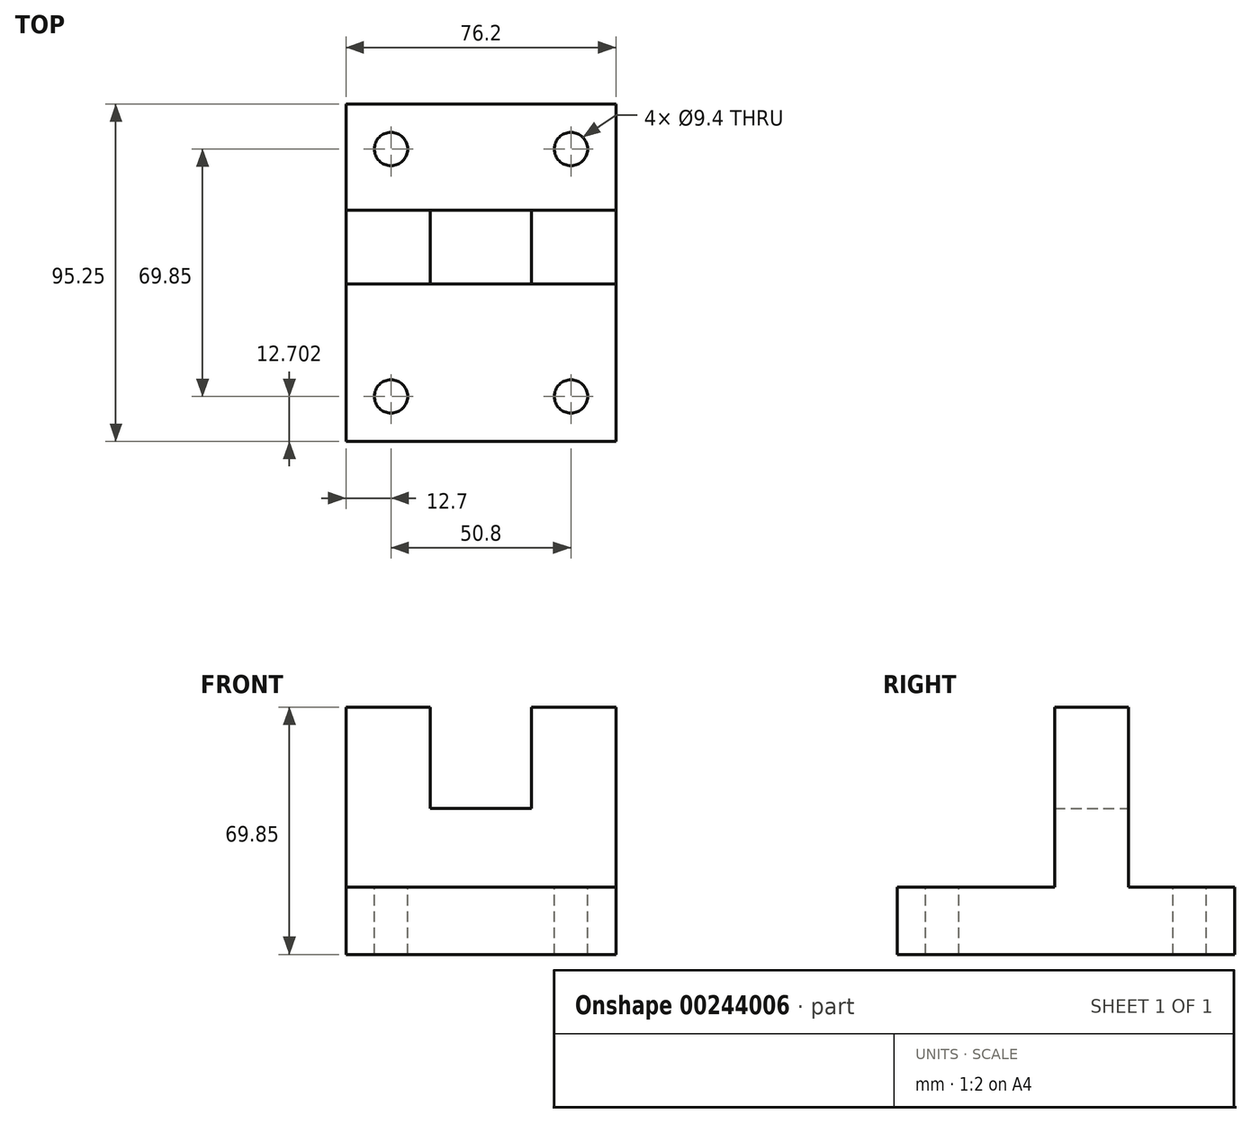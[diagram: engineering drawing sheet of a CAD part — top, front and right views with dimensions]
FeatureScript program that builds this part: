
annotation { "Feature Type Name" : "Feature", "Feature Type Description" : "" }
export const myFeature = defineFeature(function(context is Context, id is Id, definition is map)
    precondition{}
    {
        {
            var Q0;
            Q0=qCreatedBy(makeId("Front.planeOp"),FACE);
            var sketch = newSketch(context, id + "F0", { "sketchPlane" : qUnion([Q0])});
            skLineSegment(sketch, "E0.bottom", {"start": v(-52.39, 0) * mm, "end": v(-23.81, 0) * mm});
            skLineSegment(sketch, "E0.top", {"start": v(-76.2, -3.18) * mm, "end": v(0, -3.18) * mm});
            skLineSegment(sketch, "E0.left", {"start": v(-76.2, 0) * mm, "end": v(-76.2, -3.18) * mm});
            skLineSegment(sketch, "E0.right", {"start": v(0, 0) * mm, "end": v(0, -3.18) * mm});
            skLineSegment(sketch, "E1.bottom", {"start": v(-76.2, 28.58) * mm, "end": v(-52.39, 28.58) * mm});
            skLineSegment(sketch, "E1.left", {"start": v(-76.2, 28.58) * mm, "end": v(-76.2, 0) * mm});
            skLineSegment(sketch, "E1.right", {"start": v(-52.39, 28.58) * mm, "end": v(-52.39, 0) * mm});
            skLineSegment(sketch, "E2.top", {"start": v(-23.81, 28.58) * mm, "end": v(0, 28.58) * mm});
            skLineSegment(sketch, "E2.left", {"start": v(-23.81, 0) * mm, "end": v(-23.81, 28.58) * mm});
            skLineSegment(sketch, "E2.right", {"start": v(0, 0) * mm, "end": v(0, 28.58) * mm});
            skLineSegment(sketch, "E3.top", {"start": v(-76.2, -22.23) * mm, "end": v(0, -22.23) * mm});
            skLineSegment(sketch, "E3.left", {"start": v(-76.2, -3.18) * mm, "end": v(-76.2, -22.23) * mm});
            skLineSegment(sketch, "E3.right", {"start": v(0, -3.18) * mm, "end": v(0, -22.23) * mm});
            skSolve(sketch);
        }
        {
            var Q0;
            Q0 = qSketchRegion(id + "F0", true);
            extrude(context, id + "F1", {"entities" : qUnion([Q0]), "depth" : 20.83 * mm});
        }
        {
            var Q0;
            Q0=qCreatedBy(makeId("Right.planeOp"),FACE);
            var sketch = newSketch(context, id + "F2", { "sketchPlane" : qUnion([Q0])});
            skPoint(sketch, "E4.end.orphan", {"position": v(-65.73, -22.57) * mm});
            skPoint(sketch, "E5.start.orphan", {"position": v(-65.73, -41.62) * mm});
            skPoint(sketch, "E6.start.orphan", {"position": v(0, -22.57) * mm});
            skPoint(sketch, "E7.end.orphan", {"position": v(29.52, -41.62) * mm});
            skLineSegment(sketch, "E8.0", {"start": v(-20.83, -22.23) * mm, "end": v(0, -22.23) * mm});
            skLineSegment(sketch, "E9", {"start": v(-20.83, -22.23) * mm, "end": v(-65.28, -22.23) * mm});
            skLineSegment(sketch, "E10", {"start": v(-65.28, -22.23) * mm, "end": v(-65.28, -41.28) * mm});
            skLineSegment(sketch, "E11", {"start": v(-65.28, -41.28) * mm, "end": v(29.97, -41.28) * mm});
            skLineSegment(sketch, "E12", {"start": v(29.97, -41.28) * mm, "end": v(29.97, -22.23) * mm});
            skLineSegment(sketch, "E13", {"start": v(29.97, -22.23) * mm, "end": v(0, -22.23) * mm});
            skSolve(sketch);
        }
        {
            var Q0;
            Q0 = qSketchRegion(id + "F2", true);
            extrude(context, id + "F3", {"entities" : qUnion([Q0]), "operationType" : NewBodyOperationType.ADD, "oppositeDirection" : true, "depth" : 76.2 * mm});
        }
        {
            var Q0;
            Q0=qCreatedBy(makeId("Top.planeOp"),FACE);
            var sketch = newSketch(context, id + "F4", { "sketchPlane" : qUnion([Q0])});
            skCircle(sketch, "E14", {"center": v(-12.7, 17.27) * mm, "radius": 4.7 * mm});
            skCircle(sketch, "E15", {"center": v(-12.7, -52.58) * mm, "radius": 4.7 * mm});
            skLineSegment(sketch, "E16.0", {"start": v(-76.2, -65.28) * mm, "end": v(0, -65.28) * mm, "construction": true});
            skLineSegment(sketch, "E17", {"start": v(-38.1, -65.28) * mm, "end": v(-38.1, -41.38) * mm, "construction": true});
            skCircle(sketch, "E18.MirrorC", {"center": v(-63.5, -52.58) * mm, "radius": 4.7 * mm});
            skCircle(sketch, "E19.MirrorC", {"center": v(-63.5, 17.27) * mm, "radius": 4.7 * mm});
            skSolve(sketch);
        }
        {
            var Q0;
            Q0 = qSketchRegion(id + "F4", true);
            extrude(context, id + "F5", {"entities" : qUnion([Q0]), "operationType" : NewBodyOperationType.REMOVE, "endBound" : BoundingType.THROUGH_ALL, "oppositeDirection" : true, "depth" : 25.4 * mm});
        }
    });
